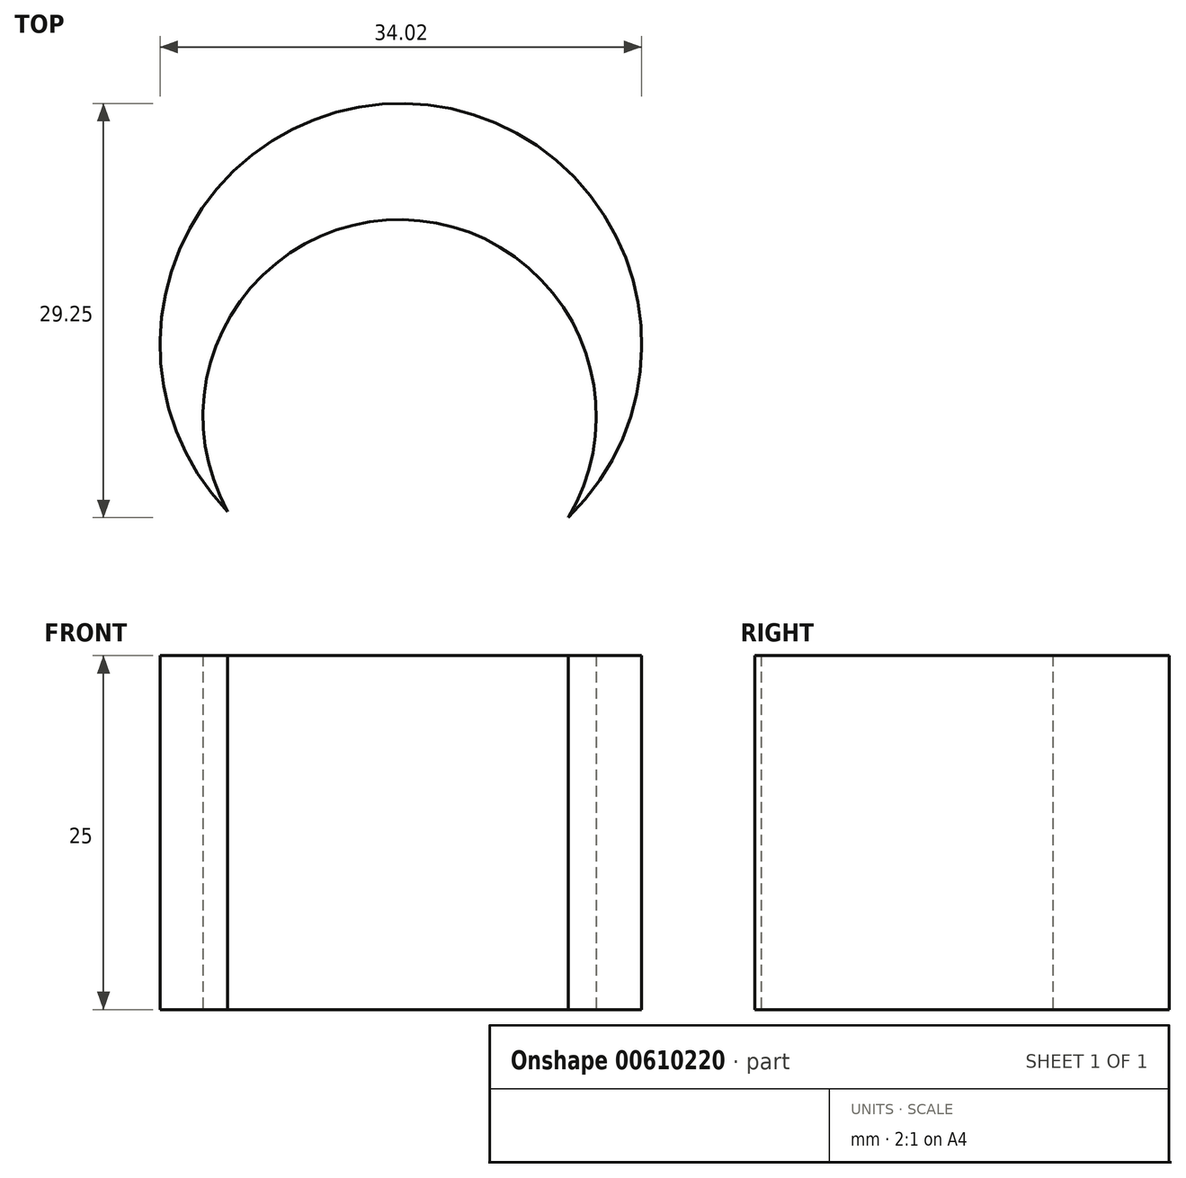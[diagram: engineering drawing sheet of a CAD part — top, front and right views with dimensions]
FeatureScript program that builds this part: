
annotation { "Feature Type Name" : "Feature", "Feature Type Description" : "" }
export const myFeature = defineFeature(function(context is Context, id is Id, definition is map)
    precondition{}
    {
        {
            var Q0;
            Q0=qCreatedBy(makeId("Top.planeOp"),FACE);
            var sketch = newSketch(context, id + "F0", { "sketchPlane" : qUnion([Q0])});
            skArc(sketch, "E0", {"start": v(-12.03, -12.03) * mm, "mid": v(8.8, 0) * mm, "end": v(-12.03, 12.03) * mm});
            skArc(sketch, "E1", {"start": v(-12.03, 12.03) * mm, "mid": v(-32.86, 0) * mm, "end": v(-12.03, -12.03) * mm});
            skCircle(sketch, "E2", {"center": v(0, 0) * mm, "radius": 17.01 * mm});
            skPoint(sketch, "E3", {"position": v(-12.03, -12.03) * mm});
            skPoint(sketch, "E4", {"position": v(-12.03, 12.03) * mm});
            skPoint(sketch, "E5", {"position": v(8.8, 0) * mm});
            skArc(sketch, "E6.1.0", {"start": v(-12.03, -12.03) * mm, "mid": v(0, -32.86) * mm, "end": v(12.03, -12.03) * mm});
            skArc(sketch, "E6.2.0", {"start": v(12.03, -12.03) * mm, "mid": v(32.86, 0) * mm, "end": v(12.03, 12.03) * mm});
            skArc(sketch, "E6.3.0", {"start": v(12.03, 12.03) * mm, "mid": v(0, 32.86) * mm, "end": v(-12.03, 12.03) * mm});
            skSolve(sketch);
        }
        {
            var Q0;
            Q0=sQuery(id+"F0.wireOp",EDGE,"E6.1.0");
            var Q1;
            Q1=sQuery(id+"F0.wireOp",EDGE,"E1");
            var Q2;
            Q2=sQuery(id+"F0.wireOp",EDGE,"E6.3.0");
            var Q3;
            Q3=sQuery(id+"F0.wireOp",EDGE,"E6.2.0");
            extrude(context, id + "F1", {"bodyType" : ToolBodyType.SURFACE, "surfaceEntities" : qUnion([Q0, Q1, Q2, Q3]), "depth" : 25 * mm, "offsetDistance" : 25 * mm});
        }
        {
            var Q0;
            {var subQ0=sQuery(id+"F0.wireOp",EDGE,"E0");Q0=makeQuery(id+"F0.imprint","IMPRINT",FACE,{"disambiguationData":[TD([[makeQuery(id+"F0.imprint","IMPRINT",EDGE,{"derivedFrom":subQ0}),-1.0]])]});}
            extrude(context, id + "F2", {"entities" : qUnion([Q0]), "depth" : 25 * mm, "offsetDistance" : 25 * mm});
        }
        {
            var Q0;
            Q0=makeQuery(id+"F2.opExtrude","SWEPT_BODY",BODY,{"disambiguationData":[OSD([sQuery(id+"F0.wireOp",EDGE,"E0"),sQuery(id+"F0.wireOp",EDGE,"E2")])]});
            var Q1;
            Q1=sQuery(id+"F0.wireOp",EDGE,"E2");
            transform(context, id + "F3", {"entities" : qUnion([Q0]), "transformType" : TransformType.ROTATION, "transformAxis" : qUnion([Q1]), "angle" : 89 * degree, "makeCopy" : false});
        }
    });
